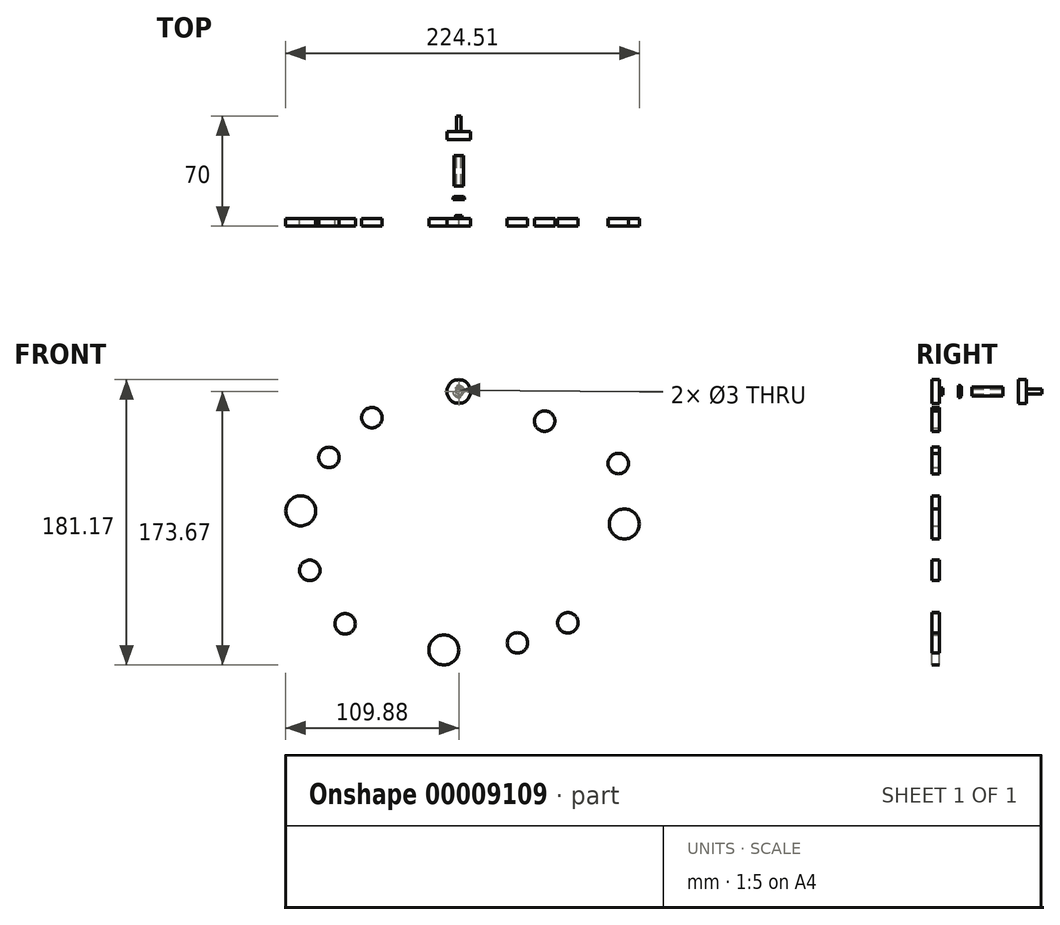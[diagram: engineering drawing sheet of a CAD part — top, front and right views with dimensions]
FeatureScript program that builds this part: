
annotation { "Feature Type Name" : "Feature", "Feature Type Description" : "" }
export const myFeature = defineFeature(function(context is Context, id is Id, definition is map)
    precondition{}
    {
        {
            var Q0;
            Q0=qCreatedBy(makeId("Front.planeOp"),FACE);
            var sketch = newSketch(context, id + "F0", { "sketchPlane" : qUnion([Q0])});
            skCircle(sketch, "E0", {"center": v(0, 0) * mm, "radius": 7.5 * mm});
            skSolve(sketch);
        }
        {
            var Q0;
            Q0 = qSketchRegion(id + "F0", true);
            extrude(context, id + "F1", {"entities" : qUnion([Q0]), "depth" : 5 * mm});
        }
        {
            var Q0;
            Q0=makeQuery(id+"F1.opExtrude","CAP_FACE",FACE,{"disambiguationData":[OSD([sQuery(id+"F0.wireOp",EDGE,"E0")])],"isStart":true});
            var sketch = newSketch(context, id + "F2", { "sketchPlane" : qUnion([Q0])});
            skCircle(sketch, "E1", {"center": v(0, 0) * mm, "radius": 2.25 * mm});
            skSolve(sketch);
        }
        {
            var Q0;
            Q0 = qSketchRegion(id + "F2", true);
            extrude(context, id + "F3", {"entities" : qUnion([Q0]), "operationType" : NewBodyOperationType.ADD, "depth" : 1.9 * mm, "hasDraft" : true, "draftAngle" : 5 * degree, "draftPullDirection" : true});
        }
        {
            var Q0;
            Q0=makeQuery(id+"F3.opExtrude","CAP_FACE",FACE,{"disambiguationData":[OSD([sQuery(id+"F2.wireOp",EDGE,"E1")])],"isStart":false});
            var sketch = newSketch(context, id + "F4", { "sketchPlane" : qUnion([Q0])});
            skCircle(sketch, "E2", {"center": v(0, 0) * mm, "radius": 1.5 * mm});
            skSolve(sketch);
        }
        {
            var Q0;
            Q0=makeQuery(id+"F3.opExtrude","CAP_FACE",FACE,{"disambiguationData":[OSD([sQuery(id+"F2.wireOp",EDGE,"E1")])],"isStart":false});
            cPlane(context, id + "F5", {"entities" : qUnion([Q0]), "cplaneType" : CPlaneType.OFFSET, "offset" : 10 * mm, "width" : 150 * mm, "height" : 150 * mm});
        }
        {
            var Q0;
            Q0=qCreatedBy(makeId("Front.planeOp"),FACE);
            cPlane(context, id + "F6", {"entities" : qUnion([Q0]), "cplaneType" : CPlaneType.OFFSET, "offset" : 40 * mm, "oppositeDirection" : true, "width" : 150 * mm, "height" : 150 * mm});
        }
        {
            var Q0;
            Q0=qCreatedBy(id+"F5.planeOp",FACE);
            var sketch = newSketch(context, id + "F7", { "sketchPlane" : qUnion([Q0])});
            skCircle(sketch, "E3", {"center": v(0, 0) * mm, "radius": 3.75 * mm});
            skSolve(sketch);
        }
        {
            var Q0;
            Q0=makeQuery(id+"F7.imprint","IMPRINT",FACE,{"disambiguationData":[TD([[makeQuery(id+"F7.imprint","IMPRINT",EDGE,{"derivedFrom":sQuery(id+"F7.wireOp",EDGE,"E3")}),1.0]])]});
            extrude(context, id + "F8", {"entities" : qUnion([Q0]), "operationType" : NewBodyOperationType.ADD, "depth" : 2 * mm});
        }
        {
            var Q0;
            Q0=makeQuery(id+"F8.opExtrude","CAP_FACE",FACE,{"disambiguationData":[OSD([sQuery(id+"F7.wireOp",EDGE,"E3")])],"isStart":false});
            var sketch = newSketch(context, id + "F9", { "sketchPlane" : qUnion([Q0])});
            skCircle(sketch, "E4.0.0", {"center": v(0, 0) * mm, "radius": 7.5 * mm});
            skCircle(sketch, "E5", {"center": v(0, 0) * mm, "radius": 1.5 * mm});
            skSolve(sketch);
        }
        {
            var Q0;
            Q0=makeQuery(id+"F9.imprint","IMPRINT",FACE,{"disambiguationData":[TD([[makeQuery(id+"F9.imprint","IMPRINT",EDGE,{"derivedFrom":sQuery(id+"F9.wireOp",EDGE,"E5")}),1.0]])]});
            extrude(context, id + "F10", {"entities" : qUnion([Q0]), "operationType" : NewBodyOperationType.REMOVE, "oppositeDirection" : true, "depth" : 2 * mm});
        }
        {
            var Q0;
            Q0=makeQuery(id+"F8.opExtrude","CAP_EDGE",EDGE,{"disambiguationData":[OSD([sQuery(id+"F7.wireOp",EDGE,"E3")])],"isStart":false});
            chamfer(context, id + "F11", {"entities" : qUnion([Q0]), "width" : .75 * mm, "tangentPropagation" : true});
        }
        {
            var Q0;
            Q0=qCreatedBy(id+"F6.planeOp",FACE);
            var sketch = newSketch(context, id + "F12", { "sketchPlane" : qUnion([Q0])});
            skCircle(sketch, "E6", {"center": v(0, 0) * mm, "radius": 3 * mm});
            skCircle(sketch, "E7.0", {"center": v(0, 0) * mm, "radius": 1.5 * mm, "construction": true});
            skCircle(sketch, "E8", {"center": v(0, 0) * mm, "radius": 1.5 * mm});
            skSolve(sketch);
        }
        {
            var Q0;
            Q0=makeQuery(id+"F12.imprint","IMPRINT",FACE,{"disambiguationData":[TD([[makeQuery(id+"F12.imprint","IMPRINT",EDGE,{"derivedFrom":sQuery(id+"F12.wireOp",EDGE,"E6")}),1.0]])]});
            extrude(context, id + "F13", {"entities" : qUnion([Q0]), "depth" : 19.5 * mm});
        }
        {
            var Q0;
            Q0=qCreatedBy(id+"F6.planeOp",FACE);
            cPlane(context, id + "F14", {"entities" : qUnion([Q0]), "cplaneType" : CPlaneType.OFFSET, "offset" : 10 * mm, "oppositeDirection" : true, "width" : 150 * mm, "height" : 150 * mm});
        }
        {
            var Q0;
            Q0=qCreatedBy(id+"F14.planeOp",FACE);
            var sketch = newSketch(context, id + "F15", { "sketchPlane" : qUnion([Q0])});
            skCircle(sketch, "E9.0.0", {"center": v(0, 0) * mm, "radius": 7.5 * mm});
            skCircle(sketch, "E10.0", {"center": v(0, 0) * mm, "radius": 3 * mm});
            skCircle(sketch, "E11.0", {"center": v(0, 0) * mm, "radius": 1.5 * mm});
            skSolve(sketch);
        }
        {
            var Q0;
            Q0=makeQuery(id+"F15.imprint","IMPRINT",FACE,{"disambiguationData":[TD([[makeQuery(id+"F15.imprint","IMPRINT",EDGE,{"derivedFrom":sQuery(id+"F15.wireOp",EDGE,"E9.0.0")}),1.0]])]});
            var Q1;
            Q1=makeQuery(id+"F15.imprint","IMPRINT",FACE,{"disambiguationData":[TD([[makeQuery(id+"F15.imprint","IMPRINT",EDGE,{"derivedFrom":sQuery(id+"F15.wireOp",EDGE,"E11.0")}),1.0]])]});
            var Q2;
            Q2=makeQuery(id+"F15.imprint","IMPRINT",FACE,{"disambiguationData":[TD([[makeQuery(id+"F15.imprint","IMPRINT",EDGE,{"derivedFrom":sQuery(id+"F15.wireOp",EDGE,"E10.0")}),1.0]])]});
            extrude(context, id + "F16", {"entities" : qUnion([Q0, Q1, Q2]), "oppositeDirection" : true, "depth" : 5 * mm});
        }
        {
            var Q0;
            Q0=makeQuery(id+"F15.imprint","IMPRINT",FACE,{"disambiguationData":[TD([[makeQuery(id+"F15.imprint","IMPRINT",EDGE,{"derivedFrom":sQuery(id+"F15.wireOp",EDGE,"E11.0")}),1.0]])]});
            extrude(context, id + "F17", {"entities" : qUnion([Q0]), "operationType" : NewBodyOperationType.ADD, "oppositeDirection" : true, "depth" : 15 * mm});
        }
        {
            var Q0;
            Q0=qCreatedBy(makeId("Front.planeOp"),FACE);
            var sketch = newSketch(context, id + "F18", { "sketchPlane" : qUnion([Q0])});
            skCircle(sketch, "E12", {"center": v(-55.22, -16.65) * mm, "radius": 6.5 * mm});
            skCircle(sketch, "E13", {"center": v(-82.46, -41.88) * mm, "radius": 6.5 * mm});
            skCircle(sketch, "E14", {"center": v(-100.38, -75.82) * mm, "radius": 9.5 * mm});
            skCircle(sketch, "E15", {"center": v(-94.62, -113.6) * mm, "radius": 6.5 * mm});
            skCircle(sketch, "E16", {"center": v(-72.21, -147.52) * mm, "radius": 6.5 * mm});
            skCircle(sketch, "E17", {"center": v(-9.47, -164.17) * mm, "radius": 9.5 * mm});
            skCircle(sketch, "E18", {"center": v(37.27, -159.69) * mm, "radius": 6.5 * mm});
            skCircle(sketch, "E19", {"center": v(69.28, -146.88) * mm, "radius": 6.5 * mm});
            skCircle(sketch, "E20", {"center": v(105.13, -84.14) * mm, "radius": 9.5 * mm});
            skCircle(sketch, "E21", {"center": v(101.3, -45.72) * mm, "radius": 6.5 * mm});
            skCircle(sketch, "E22", {"center": v(54.55, -18.83) * mm, "radius": 6.5 * mm});
            skSolve(sketch);
        }
        {
            var Q0;
            Q0=makeQuery(id+"F18.imprint","IMPRINT",FACE,{"disambiguationData":[TD([[makeQuery(id+"F18.imprint","IMPRINT",EDGE,{"derivedFrom":sQuery(id+"F18.wireOp",EDGE,"E12")}),1.0]])]});
            extrude(context, id + "F19", {"entities" : qUnion([Q0]), "depth" : 5 * mm});
        }
        {
            var Q0;
            Q0=makeQuery(id+"F18.imprint","IMPRINT",FACE,{"disambiguationData":[TD([[makeQuery(id+"F18.imprint","IMPRINT",EDGE,{"derivedFrom":sQuery(id+"F18.wireOp",EDGE,"E13")}),1.0]])]});
            extrude(context, id + "F20", {"entities" : qUnion([Q0]), "depth" : 5 * mm});
        }
        {
            var Q0;
            Q0=makeQuery(id+"F18.imprint","IMPRINT",FACE,{"disambiguationData":[TD([[makeQuery(id+"F18.imprint","IMPRINT",EDGE,{"derivedFrom":sQuery(id+"F18.wireOp",EDGE,"E14")}),1.0]])]});
            extrude(context, id + "F21", {"entities" : qUnion([Q0]), "depth" : 5 * mm});
        }
        {
            var Q0;
            Q0=makeQuery(id+"F18.imprint","IMPRINT",FACE,{"disambiguationData":[TD([[makeQuery(id+"F18.imprint","IMPRINT",EDGE,{"derivedFrom":sQuery(id+"F18.wireOp",EDGE,"E15")}),1.0]])]});
            extrude(context, id + "F22", {"entities" : qUnion([Q0]), "depth" : 5 * mm});
        }
        {
            var Q0;
            Q0=makeQuery(id+"F18.imprint","IMPRINT",FACE,{"disambiguationData":[TD([[makeQuery(id+"F18.imprint","IMPRINT",EDGE,{"derivedFrom":sQuery(id+"F18.wireOp",EDGE,"E16")}),1.0]])]});
            extrude(context, id + "F23", {"entities" : qUnion([Q0]), "depth" : 5 * mm});
        }
        {
            var Q0;
            Q0=makeQuery(id+"F18.imprint","IMPRINT",FACE,{"disambiguationData":[TD([[makeQuery(id+"F18.imprint","IMPRINT",EDGE,{"derivedFrom":sQuery(id+"F18.wireOp",EDGE,"E17")}),1.0]])]});
            extrude(context, id + "F24", {"entities" : qUnion([Q0]), "depth" : 5 * mm});
        }
        {
            var Q0;
            Q0=makeQuery(id+"F18.imprint","IMPRINT",FACE,{"disambiguationData":[TD([[makeQuery(id+"F18.imprint","IMPRINT",EDGE,{"derivedFrom":sQuery(id+"F18.wireOp",EDGE,"E18")}),1.0]])]});
            extrude(context, id + "F25", {"entities" : qUnion([Q0]), "depth" : 5 * mm});
        }
        {
            var Q0;
            Q0=makeQuery(id+"F18.imprint","IMPRINT",FACE,{"disambiguationData":[TD([[makeQuery(id+"F18.imprint","IMPRINT",EDGE,{"derivedFrom":sQuery(id+"F18.wireOp",EDGE,"E19")}),1.0]])]});
            extrude(context, id + "F26", {"entities" : qUnion([Q0]), "depth" : 5 * mm});
        }
        {
            var Q0;
            Q0=makeQuery(id+"F18.imprint","IMPRINT",FACE,{"disambiguationData":[TD([[makeQuery(id+"F18.imprint","IMPRINT",EDGE,{"derivedFrom":sQuery(id+"F18.wireOp",EDGE,"E20")}),1.0]])]});
            extrude(context, id + "F27", {"entities" : qUnion([Q0]), "depth" : 5 * mm});
        }
        {
            var Q0;
            Q0=makeQuery(id+"F18.imprint","IMPRINT",FACE,{"disambiguationData":[TD([[makeQuery(id+"F18.imprint","IMPRINT",EDGE,{"derivedFrom":sQuery(id+"F18.wireOp",EDGE,"E21")}),1.0]])]});
            extrude(context, id + "F28", {"entities" : qUnion([Q0]), "depth" : 5 * mm});
        }
        {
            var Q0;
            Q0=makeQuery(id+"F18.imprint","IMPRINT",FACE,{"disambiguationData":[TD([[makeQuery(id+"F18.imprint","IMPRINT",EDGE,{"derivedFrom":sQuery(id+"F18.wireOp",EDGE,"E22")}),1.0]])]});
            extrude(context, id + "F29", {"entities" : qUnion([Q0]), "depth" : 5 * mm});
        }
    });
